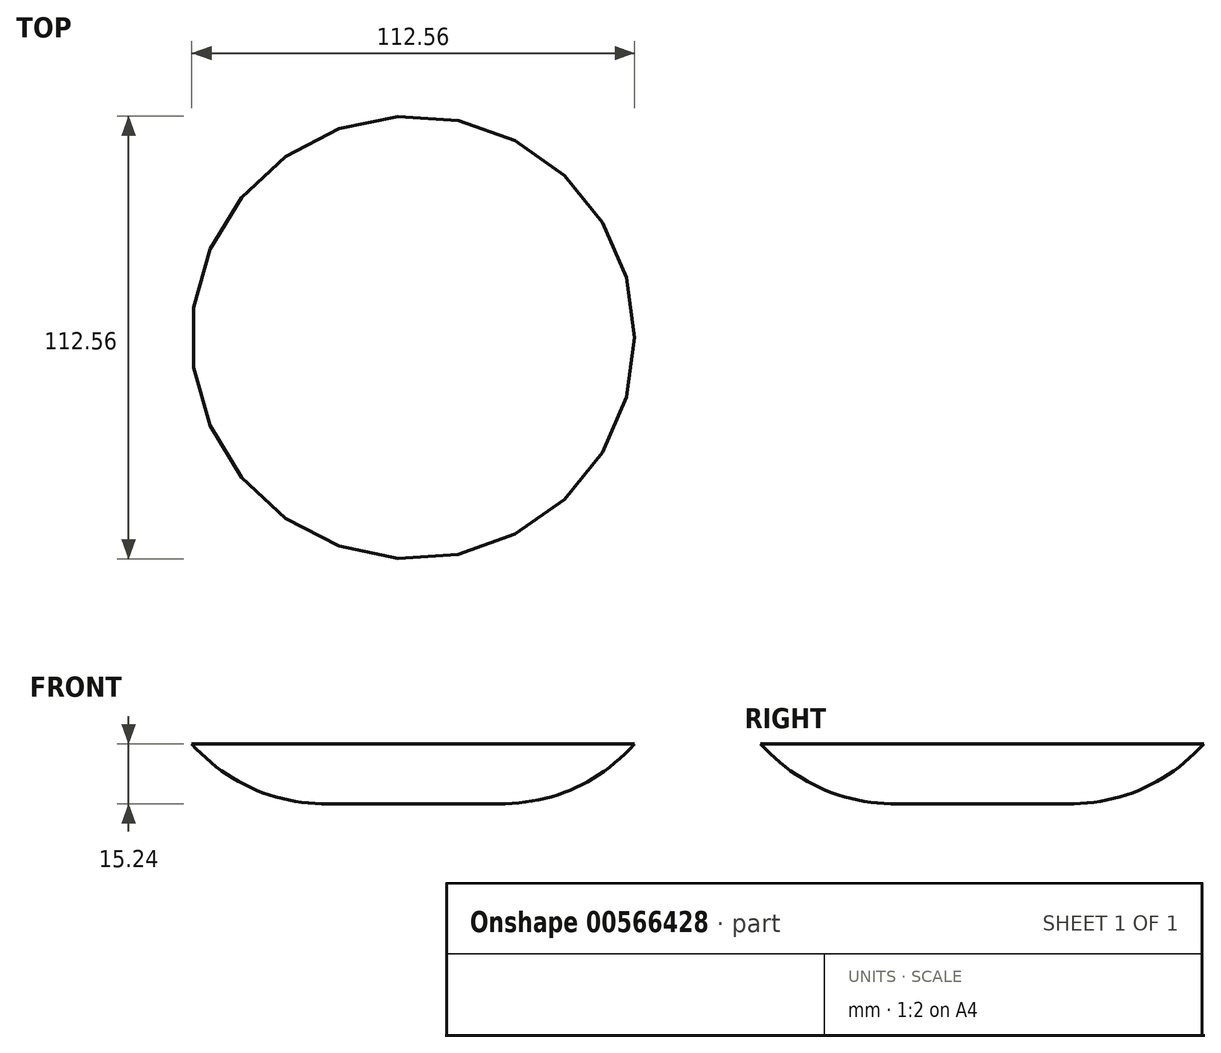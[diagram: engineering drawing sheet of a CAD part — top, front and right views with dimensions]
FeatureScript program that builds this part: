
annotation { "Feature Type Name" : "Feature", "Feature Type Description" : "" }
export const myFeature = defineFeature(function(context is Context, id is Id, definition is map)
    precondition{}
    {
        {
            var Q0;
            Q0=qCreatedBy(makeId("Top.planeOp"),FACE);
            var sketch = newSketch(context, id + "F0", { "sketchPlane" : qUnion([Q0])});
            skCircle(sketch, "E0", {"center": v(0, 0) * mm, "radius": 56.28 * mm});
            skSolve(sketch);
        }
        {
            var Q0;
            Q0=makeQuery(id+"F0.imprint","IMPRINT",FACE,{"disambiguationData":[TD([[makeQuery(id+"F0.imprint","IMPRINT",EDGE,{"derivedFrom":sQuery(id+"F0.wireOp",EDGE,"E0")}),1.0]])]});
            extrude(context, id + "F1", {"entities" : qUnion([Q0]), "oppositeDirection" : true, "depth" : 15.24 * mm, "offsetDistance" : 25.4 * mm});
        }
        {
            var Q0;
            Q0=qCreatedBy(makeId("Top.planeOp"),FACE);
            var sketch = newSketch(context, id + "F2", { "sketchPlane" : qUnion([Q0])});
            skCircle(sketch, "E1", {"center": v(0, 0) * mm, "radius": 3.3 * mm});
            skSolve(sketch);
        }
        {
            var Q0;
            Q0=makeQuery(id+"F1.opExtrude","CAP_FACE",FACE,{"disambiguationData":[OSD([sQuery(id+"F0.wireOp",EDGE,"E0")])],"isStart":false});
            fillet(context, id + "F3", {"entities" : qUnion([Q0]), "radius" : 47.22 * mm, "tangentPropagation" : true, "rho" : 0.5, "crossSection" : FilletCrossSection.CONIC, "allowEdgeOverflow" : false});
        }
        {
            var Q0;
            Q0=sQuery(id+"F2.wireOp",EDGE,"E1");
            extrude(context, id + "F4", {"bodyType" : ToolBodyType.SURFACE, "surfaceEntities" : qUnion([Q0]), "oppositeDirection" : true, "depth" : 5.84 * mm, "offsetDistance" : 25.4 * mm});
        }
    });
